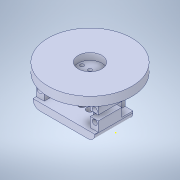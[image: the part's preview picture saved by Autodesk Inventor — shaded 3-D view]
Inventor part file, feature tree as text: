
AUTODESK INVENTOR PART (.ipt)
format: ipt  version: 2021.2 (Build 252289000, 289)  size: 312,832 bytes
history: mixed  units: mm
features: sketch x11, extrude x10, other x2, projected_geometry x2, imported_body x1
ambient origin geometry x8: Origin, YZ Plane, XZ Plane, XY Plane, X Axis, Y Axis, Z Axis, Center Point
bodies: Body1 (imported_parasolid)
feature tree (26):
  other  "Твердое тело1"
  other  "Cortar-Extruir11"
  extrude  "Выдавливание4"  Depth=10.0mm TaperAngle=0.0deg
  extrude  "Выдавливание5"  Depth=10.0mm TaperAngle=0.0deg
  extrude  "Выдавливание6"  Depth=5.0mm TaperAngle=0.0deg
  extrude  "Выдавливание11"  Depth=3.4mm
  extrude  "Выдавливание12"  Depth=3.2mm
  extrude  "Выдавливание13"  Depth=21.0mm
  extrude  "Выдавливание14"  Depth=3.8mm
  sketch  "Эскиз19"
  extrude  "Выдавливание15"  Depth=20.0mm TaperAngle=360.0deg
  extrude  "Выдавливание16"  Depth=42.0mm
  extrude  "Выдавливание17"  Depth=3.0mm TaperAngle=0.0deg
  sketch  "Эскиз6"
  projected_geometry  "Спроецированная петля1"
  sketch  "Эскиз8"
  sketch  "Эскиз9"
  sketch  "Эскиз14"
  projected_geometry  "Спроецированная петля6"
  sketch  "Эскиз15"
  sketch  "Эскиз16"
  sketch  "Эскиз18"
  sketch  "Эскиз20"
  sketch  "Эскиз21"
  sketch  "Эскиз22"
  imported_body  NMx_Import_Brep_tag  [imported B-rep: ~57 faces, bbox_mm=[71.0, 43.0, 34.0]]
